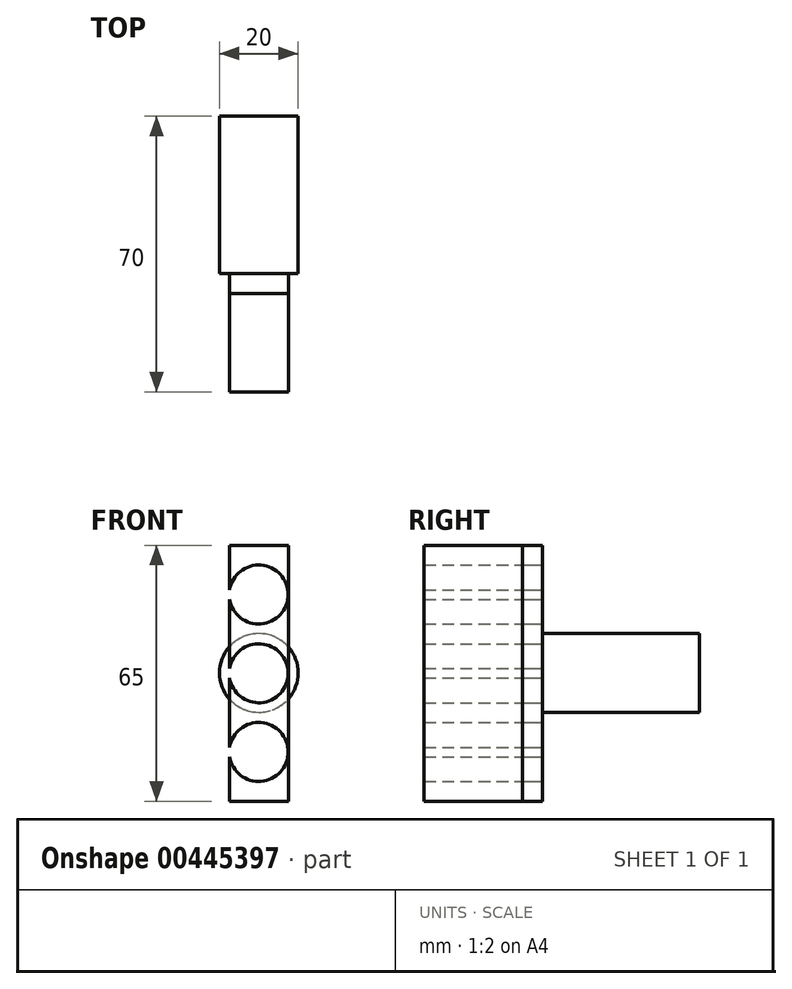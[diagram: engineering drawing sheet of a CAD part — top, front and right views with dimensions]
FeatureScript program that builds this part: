
annotation { "Feature Type Name" : "Feature", "Feature Type Description" : "" }
export const myFeature = defineFeature(function(context is Context, id is Id, definition is map)
    precondition{}
    {
        {
            var Q0;
            Q0=qCreatedBy(makeId("Front.planeOp"),FACE);
            var sketch = newSketch(context, id + "F0", { "sketchPlane" : qUnion([Q0])});
            skLineSegment(sketch, "E0.bottom", {"start": v(-21.78, 26.97) * mm, "end": v(-6.78, 26.97) * mm});
            skLineSegment(sketch, "E0.top", {"start": v(-21.78, -38.03) * mm, "end": v(-6.78, -38.03) * mm});
            skLineSegment(sketch, "E0.left", {"start": v(-21.78, 26.97) * mm, "end": v(-21.78, -38.03) * mm});
            skLineSegment(sketch, "E0.right", {"start": v(-6.78, 26.97) * mm, "end": v(-6.78, -38.03) * mm});
            skCircle(sketch, "E1", {"center": v(-14.37, -5.53) * mm, "radius": 7.5 * mm});
            skCircle(sketch, "E2", {"center": v(-14.37, 14.47) * mm, "radius": 7.5 * mm});
            skCircle(sketch, "E3", {"center": v(-14.37, -25.53) * mm, "radius": 7.5 * mm});
            skSolve(sketch);
        }
        {
            var Q0;
            {var subQ8=sQuery(id+"F0.wireOp",EDGE,"E0.bottom");Q0=makeQuery(id+"F0.imprint","IMPRINT",FACE,{"disambiguationData":[TD([[makeQuery(id+"F0.imprint","IMPRINT",EDGE,{"derivedFrom":subQ8}),-1.0]])]});}
            extrude(context, id + "F1", {"entities" : qUnion([Q0]), "depth" : 5 * mm});
        }
        {
            var Q0;
            {var subQ0=sQuery(id+"F0.wireOp",EDGE,"E2");var subQ1=sQuery(id+"F0.wireOp",EDGE,"E0.left");var subQ2=makeQuery(id+"F0.imprint","INTERSECT",VERTEX,{"disambiguationData":[OD(0.0)],"derivedFrom":[subQ1,subQ0]});Q0=makeQuery(id+"F0.imprint","IMPRINT",FACE,{"disambiguationData":[TD([[makeQuery(id+"F0.imprint","IMPRINT",EDGE,{"disambiguationData":[TD([[subQ2,-1.0]])],"derivedFrom":subQ1}),1.0]])]});}
            var Q1;
            {var subQ0=sQuery(id+"F0.wireOp",EDGE,"E1");var subQ1=sQuery(id+"F0.wireOp",EDGE,"E0.left");var subQ2=makeQuery(id+"F0.imprint","INTERSECT",VERTEX,{"disambiguationData":[OD(0.0)],"derivedFrom":[subQ1,subQ0]});Q1=makeQuery(id+"F0.imprint","IMPRINT",FACE,{"disambiguationData":[TD([[makeQuery(id+"F0.imprint","IMPRINT",EDGE,{"disambiguationData":[TD([[subQ2,-1.0]])],"derivedFrom":subQ1}),1.0]])]});}
            var Q2;
            {var subQ0=sQuery(id+"F0.wireOp",EDGE,"E3");var subQ1=sQuery(id+"F0.wireOp",EDGE,"E0.left");var subQ2=makeQuery(id+"F0.imprint","INTERSECT",VERTEX,{"disambiguationData":[OD(0.0)],"derivedFrom":[subQ1,subQ0]});Q2=makeQuery(id+"F0.imprint","IMPRINT",FACE,{"disambiguationData":[TD([[makeQuery(id+"F0.imprint","IMPRINT",EDGE,{"disambiguationData":[TD([[subQ2,-1.0]])],"derivedFrom":subQ1}),1.0]])]});}
            extrude(context, id + "F2", {"entities" : qUnion([Q0, Q1, Q2]), "depth" : 30 * mm});
        }
        {
            var Q0;
            Q0=qCreatedBy(makeId("Front.planeOp"),FACE);
            var sketch = newSketch(context, id + "F3", { "sketchPlane" : qUnion([Q0])});
            skCircle(sketch, "E4", {"center": v(-14.33, -5.44) * mm, "radius": 10 * mm});
            skSolve(sketch);
        }
        {
            var Q0;
            Q0=makeQuery(id+"F3.imprint","IMPRINT",FACE,{"disambiguationData":[TD([[makeQuery(id+"F3.imprint","IMPRINT",EDGE,{"derivedFrom":sQuery(id+"F3.wireOp",EDGE,"E4")}),1.0]])]});
            extrude(context, id + "F4", {"entities" : qUnion([Q0]), "oppositeDirection" : true, "depth" : 40 * mm});
        }
    });
